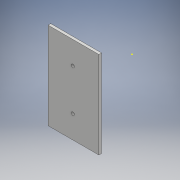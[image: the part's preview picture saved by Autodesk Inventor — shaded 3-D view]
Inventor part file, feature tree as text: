
AUTODESK INVENTOR PART (.ipt)
format: ipt  version: 2017 (Build 210142000, 142)  size: 117,760 bytes
history: native  units: mm
features: sketch x3, extrude x2
ambient origin geometry x8: Origin, YZ Plane, XZ Plane, XY Plane, X Axis, Y Axis, Z Axis, Center Point
bodies: Solid1 (feature_tree)
feature tree (5):
  extrude  "Extrusion1"  Depth=133.35mm
  extrude  "Extrusion2"  Depth=7.0mm
  sketch  "Sketch3"  dims[d7=7.9375mm d8=65.0mm d9=65.0mm d11=60.0mm d12=52.75mm d13=0.0mm]
  sketch  "Sketch1"  dims[d2=228.6mm d3=133.35mm]
  sketch  "Sketch2"  dims[d4=7.0mm d5=0.0mm d6=7.9375mm]
